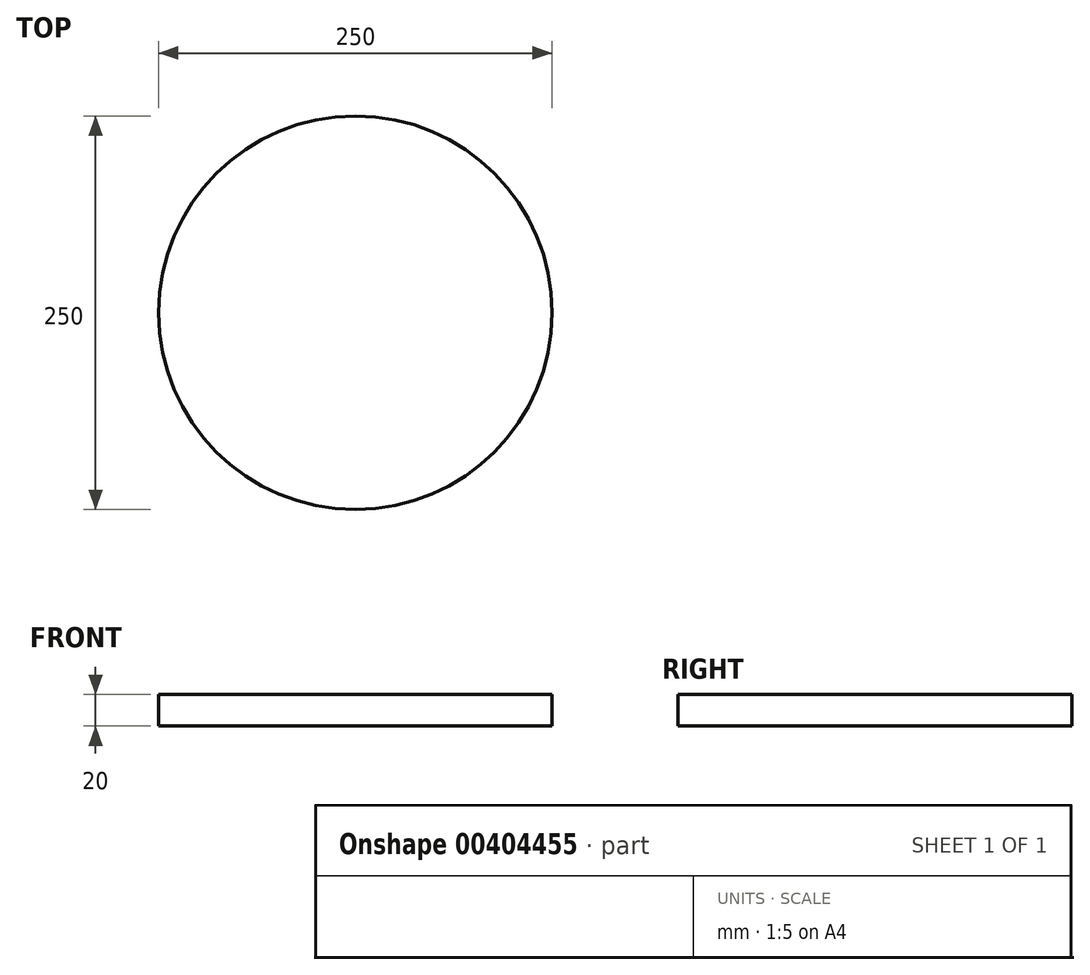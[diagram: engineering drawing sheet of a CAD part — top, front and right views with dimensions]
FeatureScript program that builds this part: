
annotation { "Feature Type Name" : "Feature", "Feature Type Description" : "" }
export const myFeature = defineFeature(function(context is Context, id is Id, definition is map)
    precondition{}
    {
        {
            var Q0;
            Q0=qCreatedBy(makeId("Top.planeOp"),FACE);
            var sketch = newSketch(context, id + "F0", { "sketchPlane" : qUnion([Q0])});
            skCircle(sketch, "E0", {"center": v(0, 0) * mm, "radius": 125 * mm});
            skSolve(sketch);
        }
        {
            var Q0;
            Q0 = qSketchRegion(id + "F0", true);
            extrude(context, id + "F1", {"entities" : qUnion([Q0]), "depth" : 20 * mm});
        }
    });
